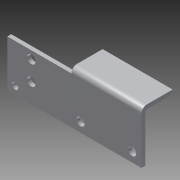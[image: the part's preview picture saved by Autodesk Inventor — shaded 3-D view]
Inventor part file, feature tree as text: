
AUTODESK INVENTOR PART (.ipt)
format: ipt  version: 2013 (Build 170138000, 138)  size: 166,912 bytes
history: native  units: in
note: dims shown in document units (in); Inventor stores cm internally (conversion verified against a paired STEP export)
features: sketch x6, other x6, sheet_metal_op x4, reference x2, extrude x1
ambient origin geometry x8: Origin, YZ Plane, XZ Plane, XY Plane, X Axis, Y Axis, Z Axis, Center Point
bodies: Solid1 (feature_tree)
feature tree (19):
  sheet_metal_op  "Face1"
  sheet_metal_op  "Flange1"
  extrude  "Extrusion1"  Depth=1.5in
  sketch  "Sketch1"  dims[d1=4.297in d2=1.5in]
  other  "Plate1"
  sketch  "Sketch2"  dims[d3=0.295in]
  other  "Plate2"
  sheet_metal_op  "Bend1"
  sheet_metal_op  "Corner1"
  sketch  "Sketch8"  dims[d4=1.181in]
  reference  "Reference1"
  reference  "Reference2"
  sketch  "Sketch10"  dims[d5=0.295in]
  sketch  "Sketch15"  dims[d8=0.125in]
  sketch  "Sketch16"  dims[d9=0.125in d10=0.0625in d11=0.25in d12=0.125in d13=1.0in d14=90.0deg d15=0.05in d16=0.5in d17=0.125in d18=0.125in d19=0.125in d20=0.0in d21=2.0in d22=2.053in d23=1.0in d24=0.0in d31=0.25in d32=0.25in d33=0.2in d34=0.125in d35=0.0in d36=0.125in d37=0.0in]
  other  "Cut1"
  other  "Cut4"
  other  "Cut5"
  other  "Definition1"
